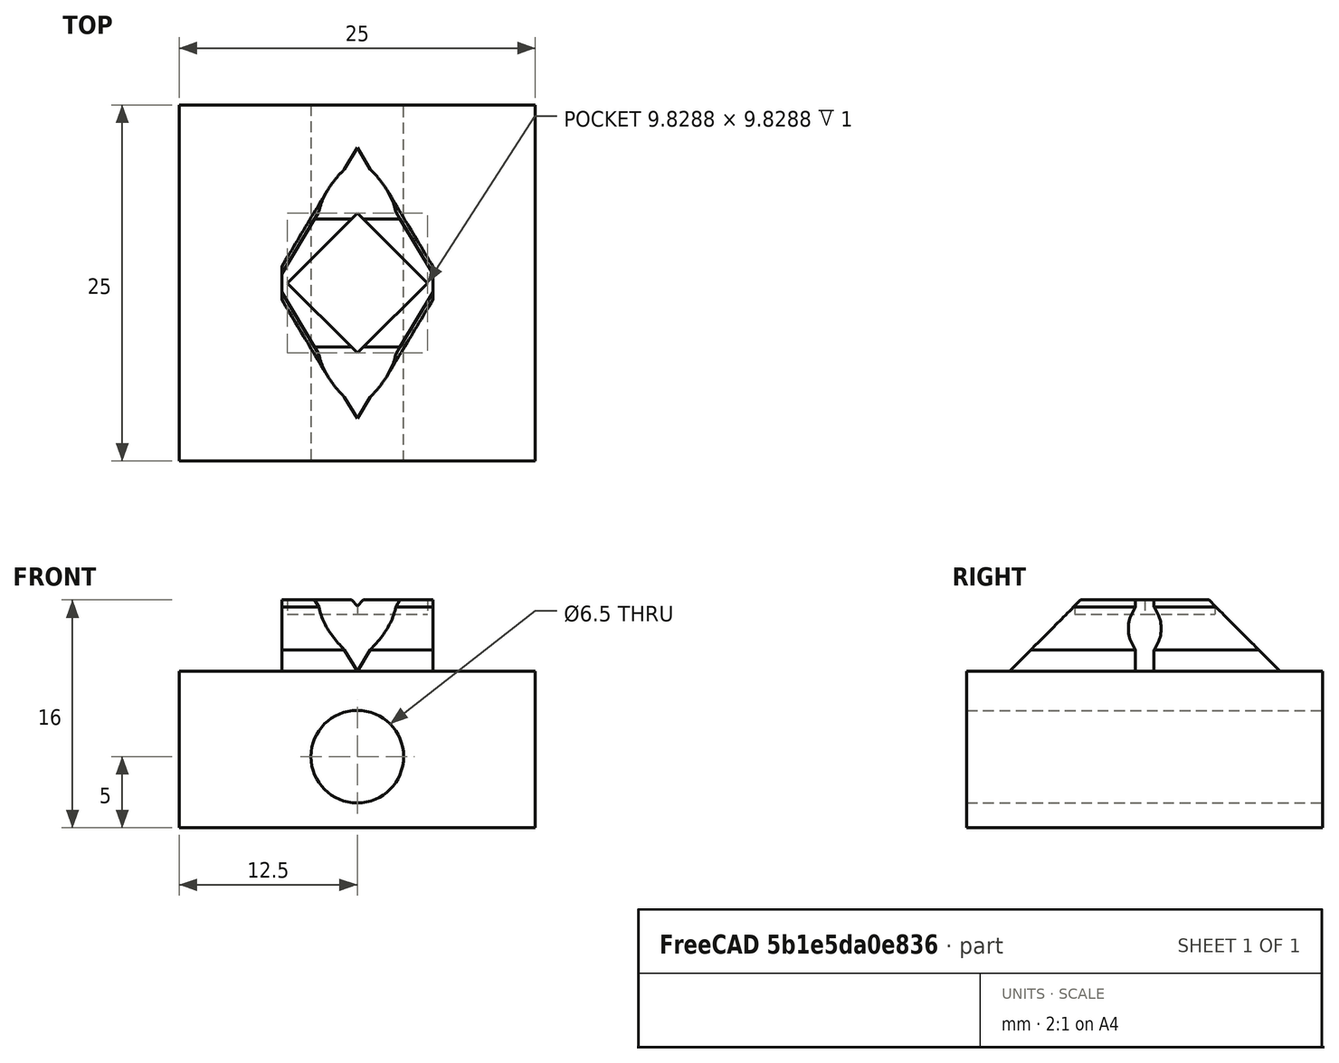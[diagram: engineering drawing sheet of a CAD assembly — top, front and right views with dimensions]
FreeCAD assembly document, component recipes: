
FREECAD ASSEMBLY — COMPONENT RECIPES ("DockLink_application_example_assembly2")

This assembly document has 2 components, labeled P0..P1 below (a component is one placed body or linked part). 1 of them carries a construction recipe — the FreeCAD feature program that regenerates the part from scratch, quoted from this document or its linked companion documents; the rest are supplied as boundary geometry only. No exploded tour is included for this assembly.
COMPONENT P0 — recipe-attached ("Body_DockLink_male", a linked part whose construction recipe lives in a companion FreeCAD document of the same project; that document's serialized recipe follows).
Construction recipe (the companion document, serialized — sketch geometry with constraints, then the solid features built on it; lengths are millimeters unless a unit is written):

FCSTD DOCUMENT  (FreeCAD 1.1R20251031 (Git shallow))
Label: DockLink_male
License: All rights reserved
LicenseURL: https://en.wikipedia.org/wiki/All_rights_reserved
objects: Sketcher::SketchObject×8, PartDesign::Pocket×3, PartDesign::Pad×2, App::Point×1, App::VarSet×1, PartDesign::AdditiveLoft×1, PartDesign::Body×1
note: 35 computed .brp shape members not serialized (recipe doc carries the construction recipe); baked Part::Feature solids carry a one-line shape summary decoded from their .brp
EXTERNAL_REF file=DockLink_female.FCStd obj=VarSet

FEATURE [App::Point] Origin001
  Role = Origin
FEATURE [Sketcher::SketchObject] Sketch  label="Sketch_Base"
  ArcFitTolerance = 1e-06
  AttachmentSupport = -> [Origin]
  ExternalTypes = [0]
  FullyConstrained = true
  MakeInternals = false
  MapMode = 5
  expr: Constraints[10] = <<DockLink_female>>#VarSet.width_printbase
  expr: Constraints[11] = <<DockLink_female>>#VarSet.width_printbase
  expr: Constraints[22] = <<DockLink_female>>#VarSet.border_vert
  expr: Constraints[23] = <<DockLink_female>>#VarSet.border_hori
  sketch-geometry (10):
    g0: LineSegment StartX=-12.5 StartY=12.5 StartZ=0 EndX=-12.5 EndY=-12.5 EndZ=0
    g1: LineSegment StartX=-12.5 StartY=-12.5 StartZ=0 EndX=12.5 EndY=-12.5 EndZ=0
    g2: LineSegment StartX=12.5 StartY=-12.5 StartZ=0 EndX=12.5 EndY=12.5 EndZ=0
    g3: LineSegment StartX=12.5 StartY=12.5 StartZ=0 EndX=-12.5 EndY=12.5 EndZ=0
    g4: GeomPoint [constr] X=0 Y=0 Z=0
    g5: LineSegment [constr] StartX=-8.5 StartY=9.5 StartZ=0 EndX=-8.5 EndY=-9.5 EndZ=0
    g6: LineSegment [constr] StartX=-8.5 StartY=-9.5 StartZ=0 EndX=8.5 EndY=-9.5 EndZ=0
    g7: LineSegment [constr] StartX=8.5 StartY=-9.5 StartZ=0 EndX=8.5 EndY=9.5 EndZ=0
    g8: LineSegment [constr] StartX=8.5 StartY=9.5 StartZ=0 EndX=-8.5 EndY=9.5 EndZ=0
    g9: GeomPoint [constr] X=0 Y=0 Z=0
  constraints (24):
    c: Coincident(g0,g1)
    c: Coincident(g1,g2)
    c: Coincident(g2,g3)
    c: Coincident(g3,g0)
    c: Vertical(g0)
    c: Vertical(g2)
    c: Horizontal(g1)
    c: Horizontal(g3)
    c: Symmetric(g2,g0,g4)
    c: Coincident(g4,g-1)
    c: DistanceX(g3,g3) = 25
    c: DistanceY(g0,g0) = 25
    c: Coincident(g5,g6)
    c: Coincident(g6,g7)
    c: Coincident(g7,g8)
    c: Coincident(g8,g5)
    c: Vertical(g5)
    c: Vertical(g7)
    c: Horizontal(g6)
    c: Horizontal(g8)
    c: Symmetric(g7,g5,g9)
    c: Coincident(g9,g4)
    c: Distance(g3,g8) = 3
    c: Distance(g2,g7) = 4
FEATURE [App::VarSet] VarSet
  diameter_feet = 6.35
  feet_gap = 0.3
  thickness_base = 6
FEATURE [PartDesign::Pad] Pad  label="Pad_Base"
  Direction = (0,0,1)
  Length = 6
  Length2 = 10
  Profile = -> Sketch
  ReferenceAxis = -> Sketch [N_Axis]
  Refine = true
  Reversed = true
  SideType = 0
  Suppressed = false
  Type = 0
  Type2 = 0
  expr: Length = VarSet.thickness_base
FEATURE [Sketcher::SketchObject] Sketch001  label="Sketch_stud"
  ArcFitTolerance = 1e-06
  AttachmentSupport = -> [Pad]
  ExternalGeometry = -> [Pad]
  ExternalTypes = [0,0,0,0]
  FullyConstrained = true
  MakeInternals = false
  MapMode = 5
  expr: Constraints[18] = <<DockLink_female>>#VarSet.width_printbase - 2 * (<<DockLink_female>>#VarSet.border_hori + <<DockLink_female>>#VarSet.thickness_clip + <<DockLink_female>>#VarSet.indent_depth_clip + 0.5 mm)
  expr: Constraints[19] = <<DockLink_female>>#VarSet.border_vert
  sketch-geometry (8):
    g0: LineSegment [constr] StartX=-12.5 StartY=12.5 StartZ=0 EndX=-12.5 EndY=-12.5 EndZ=0
    g1: LineSegment [constr] StartX=-12.5 StartY=-12.5 StartZ=0 EndX=12.5 EndY=-12.5 EndZ=0
    g2: LineSegment [constr] StartX=12.5 StartY=-12.5 StartZ=0 EndX=12.5 EndY=12.5 EndZ=0
    g3: LineSegment [constr] StartX=12.5 StartY=12.5 StartZ=0 EndX=-12.5 EndY=12.5 EndZ=0
    g4: LineSegment StartX=0 StartY=9.5 StartZ=0 EndX=-5.7 EndY=0 EndZ=0
    g5: LineSegment StartX=-5.7 StartY=0 StartZ=0 EndX=0 EndY=-9.5 EndZ=0
    g6: LineSegment StartX=0 StartY=-9.5 StartZ=0 EndX=5.7 EndY=0 EndZ=0
    g7: LineSegment StartX=5.7 StartY=0 StartZ=0 EndX=0 EndY=9.5 EndZ=0
  constraints (20):
    c: Coincident(g0,g1)
    c: Coincident(g1,g2)
    c: Coincident(g2,g3)
    c: Coincident(g3,g0)
    c: Vertical(g0)
    c: Vertical(g2)
    c: Horizontal(g1)
    c: Horizontal(g3)
    c: Coincident(g0,g-3)
    c: Coincident(g1,g-4)
    c: PointOnObject(g4,g-2)
    c: PointOnObject(g4,g-1)
    c: Coincident(g5,g4)
    c: Coincident(g6,g5)
    c: Coincident(g7,g6)
    c: Coincident(g7,g4)
    c: Symmetric(g4,g5,g-1)
    c: Symmetric(g4,g6,g-1)
    c: Distance(g4,g6) = 11.4
    c: Distance(g4,g3) = 3
FEATURE [PartDesign::Pad] Pad001  label="Pad_stud"
  BaseFeature = -> Pad
  Direction = (0,0,1)
  Length = 5
  Length2 = 10
  Profile = -> Sketch001
  ReferenceAxis = -> Sketch001 [N_Axis]
  Refine = true
  SideType = 0
  Suppressed = false
  Type = 0
  Type2 = 0
  expr: Length = <<DockLink_female>>#VarSet.thickness_base - 1 mm
FEATURE [Sketcher::SketchObject] Sketch002  label="Sketch_nose_top"
  ArcFitTolerance = 1e-06
  AttachmentOffset = pos=(0,0,-0.5) rot=(0,0,1;0rad)
  AttachmentSupport = -> [Pad001]
  ExternalGeometry = -> [Pad001]
  ExternalTypes = [0,0,0,0]
  FullyConstrained = true
  MakeInternals = false
  MapMode = 5
  Placement = pos=(0,0,4.5) rot=(0,0,1;0rad)
  expr: .AttachmentOffset.Base.z = <<DockLink_female>>#VarSet.indent_distance - <<DockLink_female>>#VarSet.thickness_base + 1 mm + <<DockLink_female>>#VarSet.indent_height / 2
FEATURE [Sketcher::SketchObject] Sketch003  label="Sketch_nose_bottom"
  ArcFitTolerance = 1e-06
  AttachmentOffset = pos=(0,0,-3.5) rot=(0,0,1;0rad)
  AttachmentSupport = -> [Pad001]
  ExternalGeometry = -> [Pad001]
  ExternalTypes = [0,0,0,0]
  FullyConstrained = true
  MakeInternals = false
  MapMode = 5
  Placement = pos=(0,0,1.5) rot=(0,0,1;0rad)
  expr: .AttachmentOffset.Base.z = <<DockLink_female>>#VarSet.indent_distance - <<DockLink_female>>#VarSet.thickness_base + 1 mm - <<DockLink_female>>#VarSet.indent_height / 2
FEATURE [Sketcher::SketchObject] Sketch004  label="Sketch_nose_middle"
  ArcFitTolerance = 1e-06
  AttachmentOffset = pos=(0,0,-2) rot=(0,0,1;0rad)
  AttachmentSupport = -> [Pad001]
  ExternalGeometry = -> [Pad001]
  ExternalTypes = [0,0,0,0]
  FullyConstrained = true
  MakeInternals = false
  MapMode = 5
  Placement = pos=(0,0,3) rot=(0,0,1;0rad)
  expr: .AttachmentOffset.Base.z = <<DockLink_female>>#VarSet.indent_distance - <<DockLink_female>>#VarSet.thickness_base + 1 mm
  expr: Constraints[11] = DockLink_female#VarSet.indent_depth_clip
  sketch-geometry (4):
    g0: LineSegment StartX=0 StartY=10 StartZ=0 EndX=-6 EndY=0 EndZ=0
    g1: LineSegment StartX=-6 StartY=0 StartZ=0 EndX=0 EndY=-10 EndZ=0
    g2: LineSegment StartX=0 StartY=-10 StartZ=0 EndX=6 EndY=0 EndZ=0
    g3: LineSegment StartX=6 StartY=0 StartZ=0 EndX=0 EndY=10 EndZ=0
  constraints (12):
    c: PointOnObject(g0,g-2)
    c: PointOnObject(g0,g-1)
    c: Coincident(g1,g0)
    c: PointOnObject(g1,g-2)
    c: Coincident(g2,g1)
    c: PointOnObject(g2,g-1)
    c: Coincident(g3,g2)
    c: Coincident(g3,g0)
    c: Parallel(g-3,g0)
    c: Parallel(g3,g-4)
    c: Parallel(g2,g-5)
    c: Distance(g0,g-6) = 0.3
FEATURE [PartDesign::AdditiveLoft] AdditiveLoft  label="AdditiveLoft_nose"
  BaseFeature = -> Pad001
  Closed = false
  Profile = -> Sketch002
  Refine = true
  Ruled = false
  Sections = -> [Sketch004,Sketch003]
  Suppressed = false
FEATURE [Sketcher::SketchObject] Sketch005  label="Sketch_feet_recess"
  ArcFitTolerance = 1e-06
  AttachmentSupport = -> [AdditiveLoft]
  ExternalTypes = [0]
  FullyConstrained = true
  MakeInternals = false
  MapMode = 5
  Placement = pos=(0,0,5) rot=(0,0,1;0rad)
  expr: Constraints[13] = VarSet.diameter_feet + 2 * VarSet.feet_gap
  sketch-geometry (5):
    g0: LineSegment StartX=0 StartY=-4.91439 StartZ=0 EndX=4.91439 EndY=9e-16 EndZ=0
    g1: LineSegment StartX=4.91439 StartY=9e-16 StartZ=0 EndX=9e-16 EndY=4.91439 EndZ=0
    g2: LineSegment StartX=9e-16 StartY=4.91439 StartZ=0 EndX=-4.91439 EndY=9e-16 EndZ=0
    g3: LineSegment StartX=-4.91439 StartY=9e-16 StartZ=0 EndX=0 EndY=-4.91439 EndZ=0
    g4: Circle [constr] CenterX=0 CenterY=0 CenterZ=0 NormalX=0 NormalY=0 NormalZ=1 AngleXU=0 Radius=4.91439
  constraints (14):
    c: Coincident(g0,g1)
    c: Coincident(g1,g2)
    c: Coincident(g2,g3)
    c: Coincident(g3,g0)
    c: Equal(g0,g1)
    c: Equal(g0,g2)
    c: Equal(g0,g3)
    c: PointOnObject(g0,g4)
    c: PointOnObject(g1,g4)
    c: PointOnObject(g2,g4)
    c: PointOnObject(g3,g4)
    c: Coincident(g4,g-1)
    c: PointOnObject(g3,g-2)
    c: Distance(g0,g2) = 6.95
FEATURE [PartDesign::Pocket] Pocket  label="Pocket_feet_recess"
  BaseFeature = -> AdditiveLoft
  Direction = (0,0,-1)
  Length = 1
  Length2 = 5
  Profile = -> Sketch005
  ReferenceAxis = -> Sketch005 [N_Axis]
  Refine = true
  SideType = 0
  Suppressed = false
  Type = 0
  Type2 = 0
FEATURE [Sketcher::SketchObject] Sketch006  label="Sketch_feet_slant"
  ArcFitTolerance = 1e-06
  AttachmentSupport = -> [Origin]
  ExternalGeometry = -> [Pocket]
  ExternalTypes = [0,0,0,0,0,0]
  FullyConstrained = true
  MakeInternals = false
  MapMode = 5
  Placement = pos=(0,0,0) rot=(0.57735,0.57735,0.57735;2.0944rad)
  expr: Constraints[20] = <<DockLink_female>>#VarSet.indent_depth_clip + 1 mm
  sketch-geometry (10):
    g0: LineSegment [constr] StartX=-9.5 StartY=1.5 StartZ=0 EndX=-9.5 EndY=5 EndZ=0
    g1: LineSegment [constr] StartX=9.5 StartY=1.5 StartZ=0 EndX=9.5 EndY=5 EndZ=0
    g2: LineSegment StartX=-10.8 StartY=0 StartZ=0 EndX=-10.8 EndY=5 EndZ=0
    g3: LineSegment StartX=-10.8 StartY=5 StartZ=0 EndX=-4.5 EndY=5 EndZ=0
    g4: LineSegment StartX=-4.5 StartY=5 StartZ=0 EndX=-9.5 EndY=0 EndZ=0
    g5: LineSegment StartX=-9.5 StartY=0 StartZ=0 EndX=-10.8 EndY=0 EndZ=0
    g6: LineSegment StartX=10.8 StartY=0 StartZ=0 EndX=10.8 EndY=5 EndZ=0
    g7: LineSegment StartX=10.8 StartY=5 StartZ=0 EndX=4.5 EndY=5 EndZ=0
    g8: LineSegment StartX=4.5 StartY=5 StartZ=0 EndX=9.5 EndY=0 EndZ=0
    g9: LineSegment StartX=9.5 StartY=0 StartZ=0 EndX=10.8 EndY=0 EndZ=0
  constraints (25):
    c: Coincident(g0,g-3)
    c: Coincident(g0,g-7)
    c: Coincident(g1,g-4)
    c: Coincident(g1,g-8)
    c: PointOnObject(g2,g-1)
    c: Vertical(g2)
    c: Coincident(g3,g2)
    c: Horizontal(g3)
    c: Coincident(g4,g3)
    c: Coincident(g4,g-3)
    c: Coincident(g5,g4)
    c: Coincident(g5,g2)
    c: PointOnObject(g6,g-1)
    c: Vertical(g6)
    c: Coincident(g7,g6)
    c: Horizontal(g7)
    c: Coincident(g8,g7)
    c: Coincident(g8,g-4)
    c: Coincident(g9,g8)
    c: Coincident(g9,g6)
    c: Distance(g0,g2) = 1.3
    c: Angle(g4,g0) = 0.785398
    c: PointOnObject(g0,g3)
    c: Equal(g3,g7)
    c: Symmetric(g3,g7,g-2)
FEATURE [PartDesign::Pocket] Pocket001
  BaseFeature = -> Pocket
  Direction = (-1,0,0)
  Length = 5
  Length2 = 5
  Profile = -> Sketch006
  ReferenceAxis = -> Sketch006 [N_Axis]
  Refine = true
  SideType = 2
  Suppressed = false
  Type = 1
  Type2 = 0
FEATURE [Sketcher::SketchObject] Sketch007
  ArcFitTolerance = 1e-06
  AttachmentSupport = -> [Pocket001]
  ExternalGeometry = -> [Pocket001]
  ExternalTypes = [0,0,0,0,0,0]
  FullyConstrained = true
  MakeInternals = false
  MapMode = 5
  sketch-geometry (6):
    g0: LineSegment StartX=-5.3072 StartY=11.5 StartZ=0 EndX=-5.3072 EndY=-11.5 EndZ=0
    g1: LineSegment StartX=-5.3072 StartY=-11.5 StartZ=0 EndX=5.3072 EndY=-11.5 EndZ=0
    g2: LineSegment StartX=5.3072 StartY=-11.5 StartZ=0 EndX=5.3072 EndY=11.5 EndZ=0
    g3: LineSegment StartX=5.3072 StartY=11.5 StartZ=0 EndX=-5.3072 EndY=11.5 EndZ=0
    g4: GeomPoint [constr] X=0 Y=0 Z=0
    g5: GeomPoint [constr] X=5.3072 Y=4e-16 Z=0
  constraints (13):
    c: Coincident(g0,g1)
    c: Coincident(g1,g2)
    c: Coincident(g2,g3)
    c: Coincident(g3,g0)
    c: Vertical(g0)
    c: Vertical(g2)
    c: Horizontal(g1)
    c: Horizontal(g3)
    c: Symmetric(g2,g0,g4)
    c: Coincident(g4,g-1)
    c: Distance(g-4,g3) = 1
    c: Symmetric(g-7,g-8,g5)
    c: PointOnObject(g5,g2)
FEATURE [PartDesign::Pocket] Pocket002
  BaseFeature = -> Pocket001
  Direction = (0,0,-1)
  Length = 5
  Length2 = 5
  Profile = -> Sketch007
  ReferenceAxis = -> Sketch007 [N_Axis]
  Refine = true
  Reversed = true
  SideType = 0
  Suppressed = false
  Type = 1
  Type2 = 0
FEATURE [PartDesign::Body] Body  label="Body_DockLink_male"
  AllowCompound = true
  Group = -> [Sketch,Pad,Sketch001,Pad001,Sketch004,Sketch002,Sketch003,AdditiveLoft,Sketch005,Pocket,Sketch006,Pocket001,Sketch007,Pocket002]
  Origin = -> Origin
  Tip = -> Pocket002
COMPONENT P1 — geometry summary ("DockLink_app_example"; no construction recipe available for this part):
  bounding box: 25.0 x 25.0 x 10.0 mm
  tessellated surface: 520 triangles
  volume: 5420 mm^3 (87% of its bounding box)
  symmetry: 2-fold rotationally symmetric about the x axis; 2-fold rotationally symmetric about the y axis; 2-fold rotationally symmetric about the z axis; mirror-symmetric across its x mid-plane, y mid-plane, z mid-plane
PROVENANCE & LICENSES
A FreeCAD (.FCStd) document from a public repository crawl; recipes are the document's own serialized feature recipes (and, for linked parts, companion documents' recipes).
License: mit.
